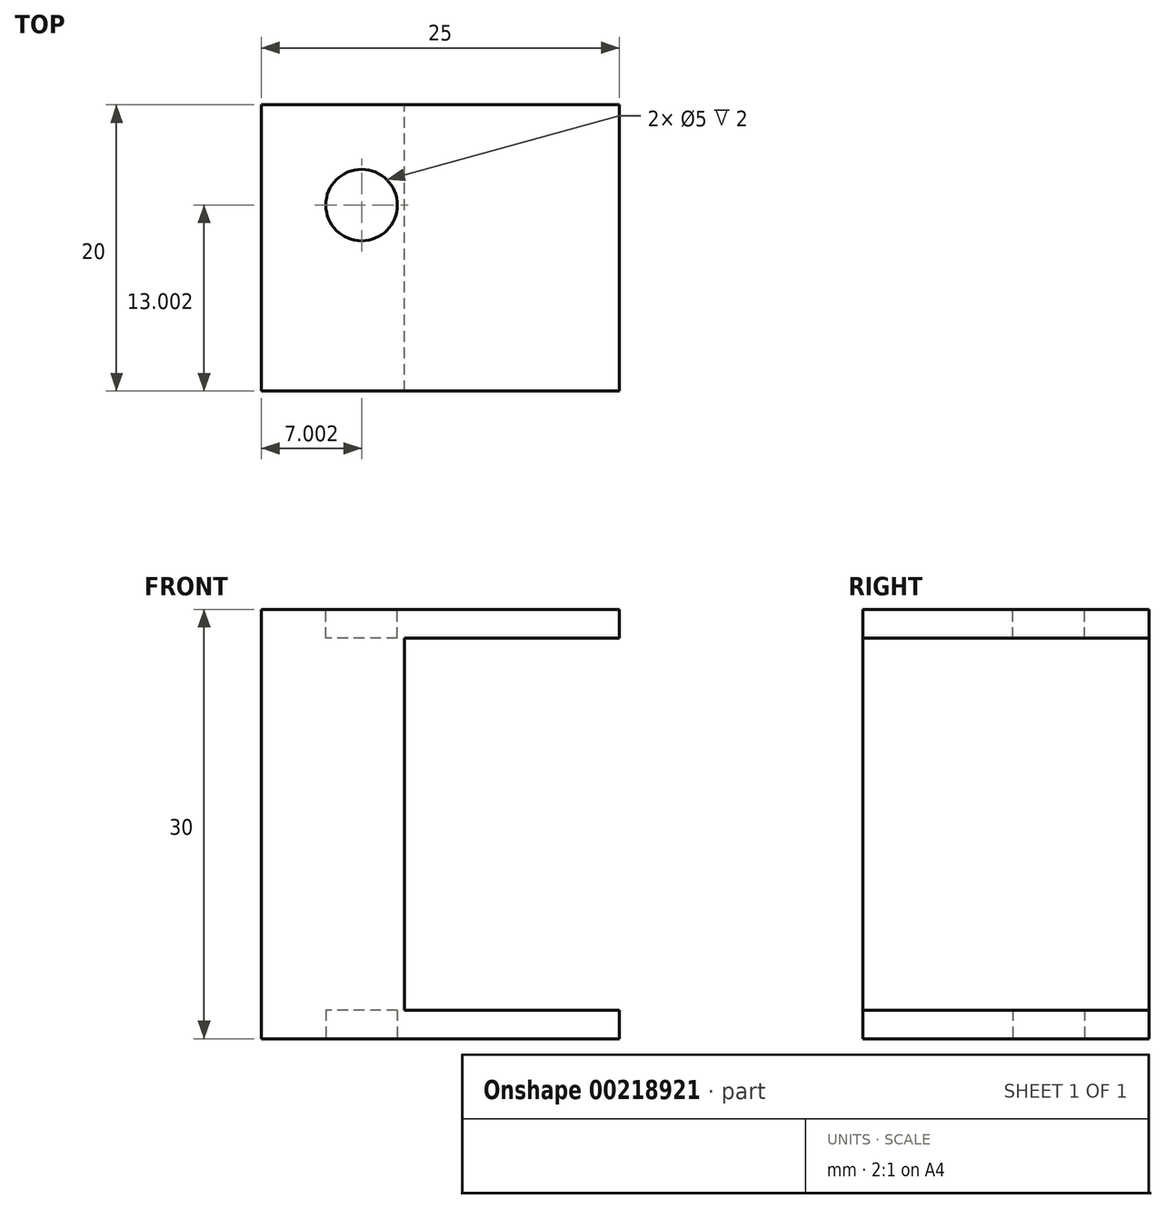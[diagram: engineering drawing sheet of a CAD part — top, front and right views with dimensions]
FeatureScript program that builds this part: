
annotation { "Feature Type Name" : "Feature", "Feature Type Description" : "" }
export const myFeature = defineFeature(function(context is Context, id is Id, definition is map)
    precondition{}
    {
        {
            var Q0;
            Q0=qCreatedBy(makeId("Top.planeOp"),FACE);
            var sketch = newSketch(context, id + "F0", { "sketchPlane" : qUnion([Q0])});
            skLineSegment(sketch, "E0.bottom", {"start": v(-15.42, 5.37) * mm, "end": v(-5.42, 5.37) * mm});
            skLineSegment(sketch, "E0.top", {"start": v(-15.42, -14.63) * mm, "end": v(-5.42, -14.63) * mm});
            skLineSegment(sketch, "E0.left", {"start": v(-15.42, 5.37) * mm, "end": v(-15.42, -14.63) * mm});
            skLineSegment(sketch, "E0.right", {"start": v(-5.42, 5.37) * mm, "end": v(-5.42, -14.63) * mm});
            skSolve(sketch);
        }
        {
            var Q0;
            Q0=qSketchRegion(id+"F0",true);
            extrude(context, id + "F1", {"entities" : qUnion([Q0]), "depth" : 30 * mm, "offsetDistance" : 25 * mm});
        }
        {
            var Q0;
            Q0=makeQuery(id+"F1.opExtrude","SWEPT_FACE",FACE,{"disambiguationData":[OSD([sQuery(id+"F0.wireOp",EDGE,"E0.right")])]});
            var sketch = newSketch(context, id + "F2", { "sketchPlane" : qUnion([Q0])});
            skLineSegment(sketch, "E1.bottom", {"start": v(-14.63, 30) * mm, "end": v(5.37, 30) * mm});
            skLineSegment(sketch, "E1.top", {"start": v(-14.63, 28) * mm, "end": v(5.37, 28) * mm});
            skLineSegment(sketch, "E1.left", {"start": v(-14.63, 30) * mm, "end": v(-14.63, 28) * mm});
            skLineSegment(sketch, "E1.right", {"start": v(5.37, 30) * mm, "end": v(5.37, 28) * mm});
            skLineSegment(sketch, "E2.bottom", {"start": v(-14.63, 0) * mm, "end": v(5.37, 0) * mm});
            skLineSegment(sketch, "E2.top", {"start": v(-14.63, 2) * mm, "end": v(5.37, 2) * mm});
            skLineSegment(sketch, "E2.left", {"start": v(-14.63, 0) * mm, "end": v(-14.63, 2) * mm});
            skLineSegment(sketch, "E2.right", {"start": v(5.37, 0) * mm, "end": v(5.37, 2) * mm});
            skSolve(sketch);
        }
        {
            var Q0;
            Q0 = qSketchRegion(id + "F2", true);
            extrude(context, id + "F3", {"entities" : qUnion([Q0]), "operationType" : NewBodyOperationType.ADD, "depth" : 15 * mm, "offsetDistance" : 25 * mm});
        }
        {
            var Q0;
            Q0=qCreatedBy(makeId("Top.planeOp"),FACE);
            var sketch = newSketch(context, id + "F4", { "sketchPlane" : qUnion([Q0])});
            skCircle(sketch, "E3", {"center": v(-8.42, -1.63) * mm, "radius": 2.5 * mm});
            skSolve(sketch);
        }
        {
            var Q0;
            Q0 = qSketchRegion(id + "F4", true);
            extrude(context, id + "F5", {"entities" : qUnion([Q0]), "operationType" : NewBodyOperationType.REMOVE, "depth" : 2 * mm, "offsetDistance" : 25 * mm});
        }
        {
            var Q0;
            Q0=makeQuery(id+"F3.boolean.opBoolean","MERGE",FACE,{"derivedFrom":[makeQuery(id+"F1.opExtrude","CAP_FACE",FACE,{"disambiguationData":[OSD([sQuery(id+"F0.wireOp",EDGE,"E0.bottom"),sQuery(id+"F0.wireOp",EDGE,"E0.top"),sQuery(id+"F0.wireOp",EDGE,"E0.left"),sQuery(id+"F0.wireOp",EDGE,"E0.right")])],"isStart":false}),makeQuery(id+"F3.opExtrude","SWEPT_FACE",FACE,{"disambiguationData":[OSD([sQuery(id+"F2.wireOp",EDGE,"E1.bottom")])]})]});
            var sketch = newSketch(context, id + "F6", { "sketchPlane" : qUnion([Q0])});
            skCircle(sketch, "E4", {"center": v(-8.42, -1.63) * mm, "radius": 2.5 * mm});
            skSolve(sketch);
        }
        {
            var Q0;
            Q0 = qSketchRegion(id + "F6", true);
            extrude(context, id + "F7", {"entities" : qUnion([Q0]), "operationType" : NewBodyOperationType.REMOVE, "oppositeDirection" : true, "depth" : 2 * mm, "offsetDistance" : 25 * mm});
        }
    });
